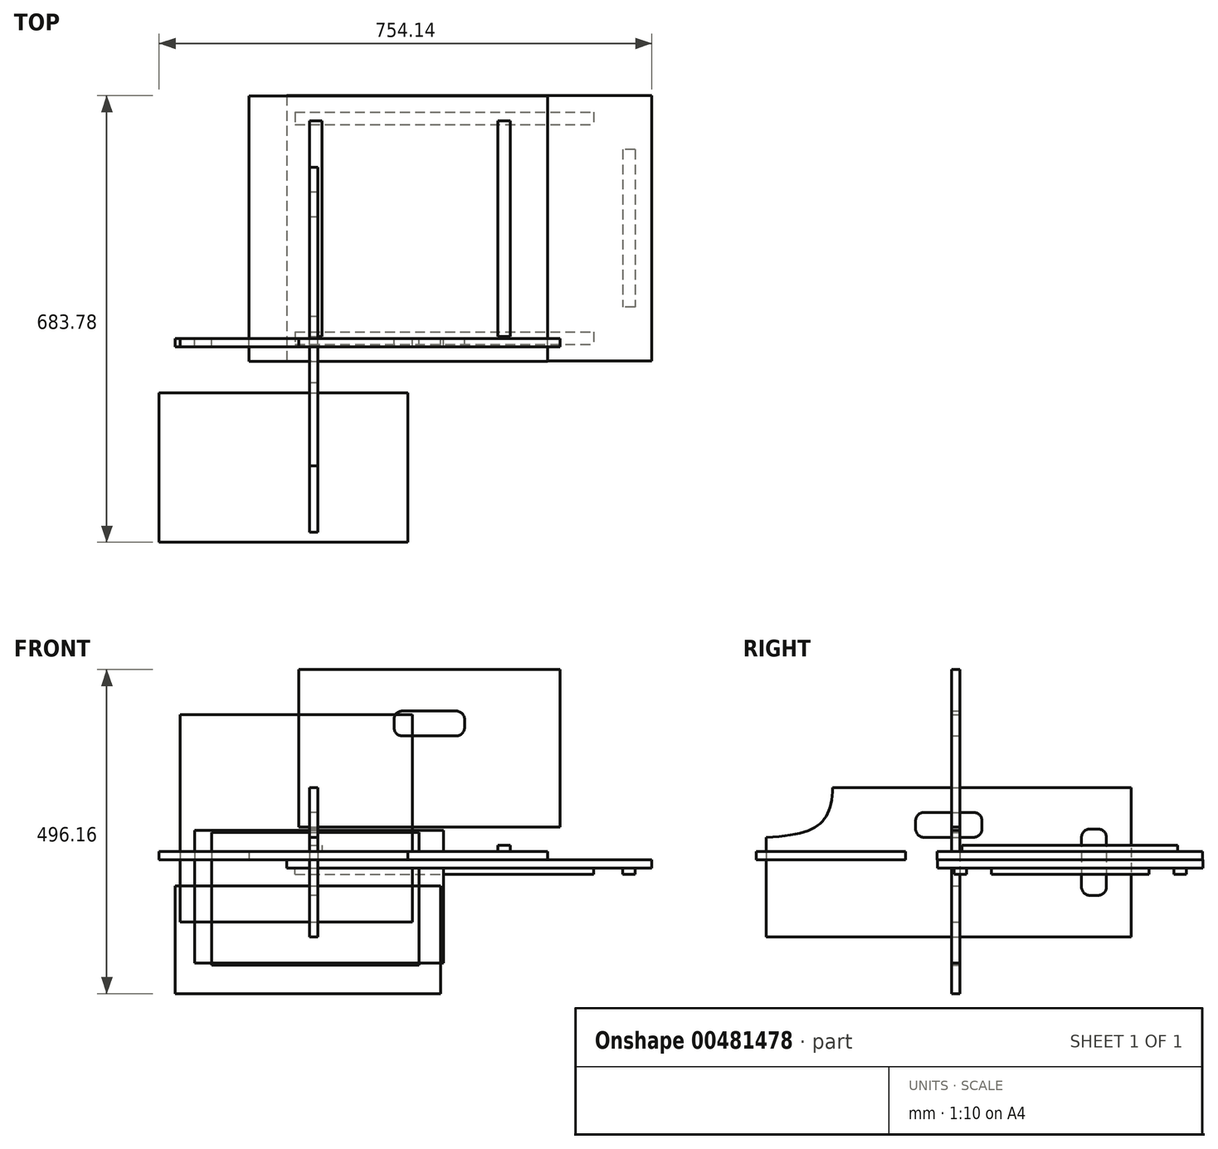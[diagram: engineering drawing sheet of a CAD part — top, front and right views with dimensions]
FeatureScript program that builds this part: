
annotation { "Feature Type Name" : "Feature", "Feature Type Description" : "" }
export const myFeature = defineFeature(function(context is Context, id is Id, definition is map)
    precondition{}
    {
        {
            var Q0;
            Q0=qCreatedBy(makeId("Top.planeOp"),FACE);
            var sketch = newSketch(context, id + "F0", { "sketchPlane" : qUnion([Q0])});
            skLineSegment(sketch, "E0.bottom", {"start": v(-34.76, 371.83) * mm, "end": v(524.04, 371.83) * mm});
            skLineSegment(sketch, "E0.top", {"start": v(-34.76, -34.57) * mm, "end": v(524.04, -34.57) * mm});
            skLineSegment(sketch, "E0.left", {"start": v(-34.76, 371.83) * mm, "end": v(-34.76, -34.57) * mm});
            skLineSegment(sketch, "E0.right", {"start": v(524.04, 371.83) * mm, "end": v(524.04, -34.57) * mm});
            skLineSegment(sketch, "E1.bottom", {"start": v(-22.06, 346.43) * mm, "end": v(435.14, 346.43) * mm});
            skLineSegment(sketch, "E1.top", {"start": v(-22.06, 327.38) * mm, "end": v(435.14, 327.38) * mm});
            skLineSegment(sketch, "E1.left", {"start": v(-22.06, 346.43) * mm, "end": v(-22.06, 327.38) * mm});
            skLineSegment(sketch, "E1.right", {"start": v(435.14, 346.43) * mm, "end": v(435.14, 327.38) * mm});
            skLineSegment(sketch, "E2.bottom", {"start": v(-22.06, 9.88) * mm, "end": v(435.14, 9.88) * mm});
            skLineSegment(sketch, "E2.top", {"start": v(-22.06, -9.17) * mm, "end": v(435.14, -9.17) * mm});
            skLineSegment(sketch, "E2.left", {"start": v(-22.06, 9.88) * mm, "end": v(-22.06, -9.17) * mm});
            skLineSegment(sketch, "E2.right", {"start": v(435.14, 9.88) * mm, "end": v(435.14, -9.17) * mm});
            skLineSegment(sketch, "E3.bottom", {"start": v(498.64, 289.28) * mm, "end": v(479.59, 289.28) * mm});
            skLineSegment(sketch, "E3.top", {"start": v(498.64, 47.98) * mm, "end": v(479.59, 47.98) * mm});
            skLineSegment(sketch, "E3.left", {"start": v(498.64, 289.28) * mm, "end": v(498.64, 47.98) * mm});
            skLineSegment(sketch, "E3.right", {"start": v(479.59, 289.28) * mm, "end": v(479.59, 47.98) * mm});
            skSolve(sketch);
        }
        {
            var Q0;
            Q0 = qSketchRegion(id + "F0", true);
            extrude(context, id + "F1", {"entities" : qUnion([Q0]), "oppositeDirection" : true, "depth" : 12.7 * mm});
        }
        {
            var Q0;
            Q0=makeQuery(id+"F0.imprint","IMPRINT",FACE,{"disambiguationData":[TD([[makeQuery(id+"F0.imprint","IMPRINT",EDGE,{"derivedFrom":sQuery(id+"F0.wireOp",EDGE,"E1.bottom")}),-1.0]])]});
            extrude(context, id + "F2", {"entities" : qUnion([Q0]), "operationType" : NewBodyOperationType.ADD, "oppositeDirection" : true, "depth" : 22.22 * mm});
        }
        {
            var Q0;
            Q0=makeQuery(id+"F0.imprint","IMPRINT",FACE,{"disambiguationData":[TD([[makeQuery(id+"F0.imprint","IMPRINT",EDGE,{"derivedFrom":sQuery(id+"F0.wireOp",EDGE,"E3.bottom")}),1.0]])]});
            extrude(context, id + "F3", {"entities" : qUnion([Q0]), "operationType" : NewBodyOperationType.ADD, "oppositeDirection" : true, "depth" : 22.22 * mm});
        }
        {
            var Q0;
            Q0=makeQuery(id+"F0.imprint","IMPRINT",FACE,{"disambiguationData":[TD([[makeQuery(id+"F0.imprint","IMPRINT",EDGE,{"derivedFrom":sQuery(id+"F0.wireOp",EDGE,"E2.bottom")}),-1.0]])]});
            extrude(context, id + "F4", {"entities" : qUnion([Q0]), "operationType" : NewBodyOperationType.ADD, "oppositeDirection" : true, "depth" : 22.22 * mm});
        }
        {
            var Q0;
            Q0=qCreatedBy(makeId("Top.planeOp"),FACE);
            var sketch = newSketch(context, id + "F5", { "sketchPlane" : qUnion([Q0])});
            skLineSegment(sketch, "E4.bottom", {"start": v(-92.2, -34.83) * mm, "end": v(365, -34.83) * mm});
            skLineSegment(sketch, "E4.top", {"start": v(-92.2, 371.57) * mm, "end": v(365, 371.57) * mm});
            skLineSegment(sketch, "E4.left", {"start": v(-92.2, -34.83) * mm, "end": v(-92.2, 371.57) * mm});
            skLineSegment(sketch, "E4.right", {"start": v(365, -34.83) * mm, "end": v(365, 371.57) * mm});
            skLineSegment(sketch, "E5.bottom", {"start": v(0, 333.47) * mm, "end": v(19.05, 333.47) * mm});
            skLineSegment(sketch, "E5.top", {"start": v(0, 3.27) * mm, "end": v(19.05, 3.27) * mm});
            skLineSegment(sketch, "E5.left", {"start": v(0, 333.47) * mm, "end": v(0, 3.27) * mm});
            skLineSegment(sketch, "E5.right", {"start": v(19.05, 333.47) * mm, "end": v(19.05, 3.27) * mm});
            skLineSegment(sketch, "E6.bottom", {"start": v(288.8, 333.47) * mm, "end": v(307.85, 333.47) * mm});
            skLineSegment(sketch, "E6.top", {"start": v(288.8, 3.27) * mm, "end": v(307.85, 3.27) * mm});
            skLineSegment(sketch, "E6.left", {"start": v(288.8, 333.47) * mm, "end": v(288.8, 3.27) * mm});
            skLineSegment(sketch, "E6.right", {"start": v(307.85, 333.47) * mm, "end": v(307.85, 3.27) * mm});
            skSolve(sketch);
        }
        {
            var Q0;
            Q0=makeQuery(id+"F5.imprint","IMPRINT",FACE,{"disambiguationData":[TD([[makeQuery(id+"F5.imprint","IMPRINT",EDGE,{"derivedFrom":sQuery(id+"F5.wireOp",EDGE,"E4.bottom")}),1.0]])]});
            extrude(context, id + "F6", {"entities" : qUnion([Q0]), "depth" : 12.7 * mm});
        }
        {
            var Q0;
            Q0=makeQuery(id+"F5.imprint","IMPRINT",FACE,{"disambiguationData":[TD([[makeQuery(id+"F5.imprint","IMPRINT",EDGE,{"derivedFrom":sQuery(id+"F5.wireOp",EDGE,"E5.bottom")}),-1.0]])]});
            extrude(context, id + "F7", {"entities" : qUnion([Q0]), "operationType" : NewBodyOperationType.ADD, "depth" : 22.22 * mm, "offsetDistance" : 25.4 * mm});
        }
        {
            var Q0;
            Q0=makeQuery(id+"F5.imprint","IMPRINT",FACE,{"disambiguationData":[TD([[makeQuery(id+"F5.imprint","IMPRINT",EDGE,{"derivedFrom":sQuery(id+"F5.wireOp",EDGE,"E6.bottom")}),-1.0]])]});
            extrude(context, id + "F8", {"entities" : qUnion([Q0]), "operationType" : NewBodyOperationType.ADD, "depth" : 22.22 * mm, "offsetDistance" : 25.4 * mm});
        }
        {
            var Q0;
            Q0=qCreatedBy(makeId("Front.planeOp"),FACE);
            var sketch = newSketch(context, id + "F9", { "sketchPlane" : qUnion([Q0])});
            skLineSegment(sketch, "E7.bottom", {"start": v(-205.72, -39.64) * mm, "end": v(200.68, -39.64) * mm});
            skLineSegment(sketch, "E7.top", {"start": v(-205.72, -204.74) * mm, "end": v(200.68, -204.74) * mm});
            skLineSegment(sketch, "E7.left", {"start": v(-205.72, -39.64) * mm, "end": v(-205.72, -204.74) * mm});
            skLineSegment(sketch, "E7.right", {"start": v(200.68, -39.64) * mm, "end": v(200.68, -204.74) * mm});
            skSolve(sketch);
        }
        {
            var Q0;
            Q0 = qSketchRegion(id + "F9", true);
            extrude(context, id + "F10", {"entities" : qUnion([Q0]), "depth" : 12.7 * mm});
        }
        {
            var Q0;
            Q0=qCreatedBy(makeId("Right.planeOp"),FACE);
            var sketch = newSketch(context, id + "F11", { "sketchPlane" : qUnion([Q0])});
            skLineSegment(sketch, "E8.bottom", {"start": v(-194.93, 110.81) * mm, "end": v(262.27, 110.81) * mm});
            skLineSegment(sketch, "E8.top", {"start": v(-296.53, -117.79) * mm, "end": v(262.27, -117.79) * mm});
            skLineSegment(sketch, "E8.left", {"start": v(-296.53, 34.61) * mm, "end": v(-296.53, -117.79) * mm});
            skLineSegment(sketch, "E8.right", {"start": v(262.27, 110.81) * mm, "end": v(262.27, -117.79) * mm});
            skFitSpline(sketch, "E9", {"points": [v(-296.53, 34.61) * mm, v(-194.93, 110.81) * mm], "startDerivative": vector(242.22, 10.76) * mm, "endDerivative": vector(3.85, 159.82) * mm});
            skLineSegment(sketch, "E10.bottom", {"start": v(-55.23, 72.71) * mm, "end": v(20.97, 72.71) * mm});
            skLineSegment(sketch, "E10.top", {"start": v(-55.23, 34.61) * mm, "end": v(20.97, 34.61) * mm});
            skLineSegment(sketch, "E10.left", {"start": v(-67.93, 60.01) * mm, "end": v(-67.93, 47.31) * mm});
            skLineSegment(sketch, "E10.right", {"start": v(33.67, 60.01) * mm, "end": v(33.67, 47.31) * mm});
            skLineSegment(sketch, "E11.bottom", {"start": v(198.77, 47.31) * mm, "end": v(211.47, 47.31) * mm});
            skLineSegment(sketch, "E11.top", {"start": v(198.77, -54.29) * mm, "end": v(211.47, -54.29) * mm});
            skLineSegment(sketch, "E11.left", {"start": v(186.07, 34.61) * mm, "end": v(186.07, -41.59) * mm});
            skLineSegment(sketch, "E11.right", {"start": v(224.17, 34.61) * mm, "end": v(224.17, -41.59) * mm});
            skPoint(sketch, "E12.visualSharp", {"position": v(-67.93, 72.71) * mm});
            skArc(sketch, "E12.filletArc", {"start": v(-55.23, 72.71) * mm, "mid": v(-64.21, 69) * mm, "end": v(-67.93, 60.01) * mm});
            skPoint(sketch, "E13.visualSharp", {"position": v(-67.93, 34.61) * mm});
            skArc(sketch, "E13.filletArc", {"start": v(-67.93, 47.31) * mm, "mid": v(-64.21, 38.33) * mm, "end": v(-55.23, 34.61) * mm});
            skPoint(sketch, "E14.visualSharp", {"position": v(33.67, 72.71) * mm});
            skArc(sketch, "E14.filletArc", {"start": v(33.67, 60.01) * mm, "mid": v(29.95, 69) * mm, "end": v(20.97, 72.71) * mm});
            skPoint(sketch, "E15.visualSharp", {"position": v(33.67, 34.61) * mm});
            skArc(sketch, "E15.filletArc", {"start": v(20.97, 34.61) * mm, "mid": v(29.95, 38.33) * mm, "end": v(33.67, 47.31) * mm});
            skPoint(sketch, "E16.visualSharp", {"position": v(186.07, 47.31) * mm});
            skArc(sketch, "E16.filletArc", {"start": v(198.77, 47.31) * mm, "mid": v(189.79, 43.6) * mm, "end": v(186.07, 34.61) * mm});
            skPoint(sketch, "E17.visualSharp", {"position": v(224.17, 47.31) * mm});
            skArc(sketch, "E17.filletArc", {"start": v(224.17, 34.61) * mm, "mid": v(220.45, 43.6) * mm, "end": v(211.47, 47.31) * mm});
            skPoint(sketch, "E18.visualSharp", {"position": v(186.07, -54.29) * mm});
            skArc(sketch, "E18.filletArc", {"start": v(186.07, -41.59) * mm, "mid": v(189.79, -50.57) * mm, "end": v(198.77, -54.29) * mm});
            skPoint(sketch, "E19.visualSharp", {"position": v(224.17, -54.29) * mm});
            skArc(sketch, "E19.filletArc", {"start": v(211.47, -54.29) * mm, "mid": v(220.45, -50.57) * mm, "end": v(224.17, -41.59) * mm});
            skLineSegment(sketch, "E20.top", {"start": v(-106.03, 110.81) * mm, "end": v(-86.98, 110.81) * mm});
            skLineSegment(sketch, "E21.bottom", {"start": v(205.12, 110.81) * mm, "end": v(186.07, 110.81) * mm});
            skLineSegment(sketch, "E22.bottom", {"start": v(-283.83, -117.79) * mm, "end": v(173.37, -117.79) * mm});
            skLineSegment(sketch, "E23.bottom", {"start": v(217.82, -117.79) * mm, "end": v(236.87, -117.79) * mm});
            skSolve(sketch);
        }
        {
            var Q0;
            Q0=makeQuery(id+"F11.imprint","IMPRINT",FACE,{"disambiguationData":[TD([[makeQuery(id+"F11.imprint","IMPRINT",EDGE,{"derivedFrom":sQuery(id+"F11.wireOp",EDGE,"E8.bottom")}),-1.0]])]});
            extrude(context, id + "F12", {"entities" : qUnion([Q0]), "depth" : 12.7 * mm});
        }
        {
            var Q0;
            Q0=qCreatedBy(makeId("Top.planeOp"),FACE);
            var sketch = newSketch(context, id + "F13", { "sketchPlane" : qUnion([Q0])});
            skLineSegment(sketch, "E24.bottom", {"start": v(-230.1, -311.95) * mm, "end": v(150.9, -311.95) * mm});
            skLineSegment(sketch, "E24.top", {"start": v(-230.1, -83.35) * mm, "end": v(150.9, -83.35) * mm});
            skLineSegment(sketch, "E24.left", {"start": v(-230.1, -311.95) * mm, "end": v(-230.1, -83.35) * mm});
            skLineSegment(sketch, "E24.right", {"start": v(150.9, -311.95) * mm, "end": v(150.9, -83.35) * mm});
            skSolve(sketch);
        }
        {
            var Q0;
            Q0 = qSketchRegion(id + "F13", true);
            extrude(context, id + "F14", {"entities" : qUnion([Q0]), "depth" : 12.7 * mm});
        }
        {
            var Q0;
            Q0=qCreatedBy(makeId("Front.planeOp"),FACE);
            var sketch = newSketch(context, id + "F15", { "sketchPlane" : qUnion([Q0])});
            skLineSegment(sketch, "E25.bottom", {"start": v(-16.5, 291.42) * mm, "end": v(383.54, 291.42) * mm});
            skLineSegment(sketch, "E25.top", {"start": v(-16.5, 50.12) * mm, "end": v(383.54, 50.12) * mm});
            skLineSegment(sketch, "E25.left", {"start": v(-16.5, 291.42) * mm, "end": v(-16.5, 50.12) * mm});
            skLineSegment(sketch, "E25.right", {"start": v(383.54, 291.42) * mm, "end": v(383.54, 50.12) * mm});
            skLineSegment(sketch, "E26.bottom", {"start": v(142.24, 227.92) * mm, "end": v(224.8, 227.92) * mm});
            skLineSegment(sketch, "E26.top", {"start": v(142.24, 189.82) * mm, "end": v(224.8, 189.82) * mm});
            skLineSegment(sketch, "E26.left", {"start": v(129.54, 215.22) * mm, "end": v(129.54, 202.52) * mm});
            skLineSegment(sketch, "E26.right", {"start": v(237.5, 215.22) * mm, "end": v(237.5, 202.52) * mm});
            skPoint(sketch, "E27.visualSharp", {"position": v(129.54, 227.92) * mm});
            skArc(sketch, "E27.filletArc", {"start": v(142.24, 227.92) * mm, "mid": v(133.26, 224.2) * mm, "end": v(129.54, 215.22) * mm});
            skPoint(sketch, "E28.visualSharp", {"position": v(129.54, 189.82) * mm});
            skArc(sketch, "E28.filletArc", {"start": v(129.54, 202.52) * mm, "mid": v(133.26, 193.54) * mm, "end": v(142.24, 189.82) * mm});
            skPoint(sketch, "E29.visualSharp", {"position": v(237.5, 189.82) * mm});
            skArc(sketch, "E29.filletArc", {"start": v(224.8, 189.82) * mm, "mid": v(233.77, 193.54) * mm, "end": v(237.5, 202.52) * mm});
            skPoint(sketch, "E30.visualSharp", {"position": v(237.5, 227.92) * mm});
            skArc(sketch, "E30.filletArc", {"start": v(237.5, 215.22) * mm, "mid": v(233.77, 224.2) * mm, "end": v(224.8, 227.92) * mm});
            skSolve(sketch);
        }
        {
            var Q0;
            Q0=makeQuery(id+"F15.imprint","IMPRINT",FACE,{"disambiguationData":[TD([[makeQuery(id+"F15.imprint","IMPRINT",EDGE,{"derivedFrom":sQuery(id+"F15.wireOp",EDGE,"E25.bottom")}),-1.0]])]});
            extrude(context, id + "F16", {"entities" : qUnion([Q0]), "depth" : 12.7 * mm});
        }
        {
            var Q0;
            Q0=qCreatedBy(makeId("Front.planeOp"),FACE);
            var sketch = newSketch(context, id + "F17", { "sketchPlane" : qUnion([Q0])});
            skLineSegment(sketch, "E31.bottom", {"start": v(-149.81, 42.28) * mm, "end": v(167.69, 42.28) * mm});
            skLineSegment(sketch, "E31.top", {"start": v(-149.81, -160.92) * mm, "end": v(167.69, -160.92) * mm});
            skLineSegment(sketch, "E31.left", {"start": v(-149.81, 42.28) * mm, "end": v(-149.81, -160.92) * mm});
            skLineSegment(sketch, "E31.right", {"start": v(167.69, 42.28) * mm, "end": v(167.69, -160.92) * mm});
            skSolve(sketch);
        }
        {
            var Q0;
            Q0 = qSketchRegion(id + "F17", true);
            extrude(context, id + "F18", {"entities" : qUnion([Q0]), "depth" : 12.7 * mm});
        }
        {
            var Q0;
            Q0=qCreatedBy(makeId("Front.planeOp"),FACE);
            var sketch = newSketch(context, id + "F19", { "sketchPlane" : qUnion([Q0])});
            skLineSegment(sketch, "E32.bottom", {"start": v(-175.81, 45.04) * mm, "end": v(205.19, 45.04) * mm});
            skLineSegment(sketch, "E32.top", {"start": v(-175.81, -158.16) * mm, "end": v(205.19, -158.16) * mm});
            skLineSegment(sketch, "E32.left", {"start": v(-175.81, 45.04) * mm, "end": v(-175.81, -158.16) * mm});
            skLineSegment(sketch, "E32.right", {"start": v(205.19, 45.04) * mm, "end": v(205.19, -158.16) * mm});
            skSolve(sketch);
        }
        {
            var Q0;
            Q0 = qSketchRegion(id + "F19", true);
            extrude(context, id + "F20", {"entities" : qUnion([Q0]), "depth" : 12.7 * mm});
        }
        {
            var Q0;
            Q0=qCreatedBy(makeId("Front.planeOp"),FACE);
            var sketch = newSketch(context, id + "F21", { "sketchPlane" : qUnion([Q0])});
            skLineSegment(sketch, "E33.bottom", {"start": v(-197.73, 222.65) * mm, "end": v(157.87, 222.65) * mm});
            skLineSegment(sketch, "E33.top", {"start": v(-197.73, -94.85) * mm, "end": v(157.87, -94.85) * mm});
            skLineSegment(sketch, "E33.left", {"start": v(-197.73, 222.65) * mm, "end": v(-197.73, -94.85) * mm});
            skLineSegment(sketch, "E33.right", {"start": v(157.87, 222.65) * mm, "end": v(157.87, -94.85) * mm});
            skSolve(sketch);
        }
        {
            var Q0;
            Q0=makeQuery(id+"F21.imprint","IMPRINT",FACE,{"disambiguationData":[TD([[makeQuery(id+"F21.imprint","IMPRINT",EDGE,{"derivedFrom":sQuery(id+"F21.wireOp",EDGE,"E33.bottom")}),-1.0]])]});
            extrude(context, id + "F22", {"entities" : qUnion([Q0]), "depth" : 12.7 * mm});
        }
    });
